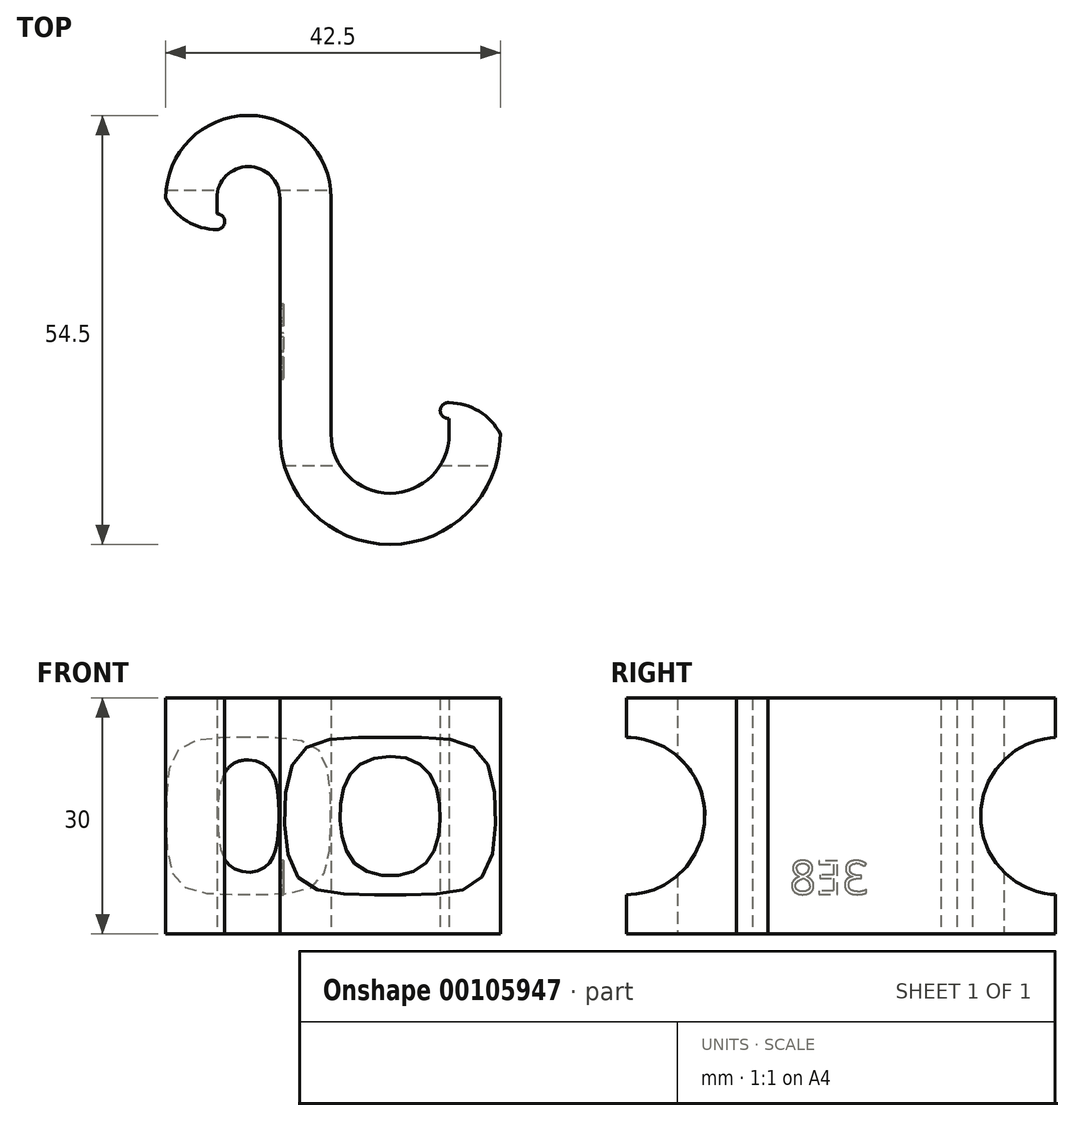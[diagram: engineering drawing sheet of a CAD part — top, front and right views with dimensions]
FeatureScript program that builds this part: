
annotation { "Feature Type Name" : "Feature", "Feature Type Description" : "" }
export const myFeature = defineFeature(function(context is Context, id is Id, definition is map)
    precondition{}
    {
        {
            var Q0;
            Q0=qCreatedBy(makeId("Top.planeOp"),FACE);
            var sketch = newSketch(context, id + "F0", { "sketchPlane" : qUnion([Q0])});
            skLineSegment(sketch, "E0", {"start": v(-4, 0) * mm, "end": v(4, 0) * mm, "construction": true});
            skLineSegment(sketch, "E1", {"start": v(-4, 0) * mm, "end": v(-4, -4) * mm, "construction": true});
            skArc(sketch, "E2", {"start": v(4, 0) * mm, "mid": v(0, 4) * mm, "end": v(-4, 0) * mm});
            skLineSegment(sketch, "E3", {"start": v(-4, -4) * mm, "end": v(-8, -4) * mm, "construction": true});
            skArc(sketch, "E4", {"start": v(10.5, 0) * mm, "mid": v(0, 10.5) * mm, "end": v(-10.5, 0) * mm});
            skLineSegment(sketch, "E5", {"start": v(10.5, 0) * mm, "end": v(10.5, -30) * mm});
            skLineSegment(sketch, "E6", {"start": v(4, -30) * mm, "end": v(10.5, -30) * mm, "construction": true});
            skArc(sketch, "E7", {"start": v(-4, -4) * mm, "mid": v(-3, -3) * mm, "end": v(-4, -2) * mm});
            skLineSegment(sketch, "E8", {"start": v(-4, -2) * mm, "end": v(-4, 0) * mm});
            skArc(sketch, "E9", {"start": v(-10.5, 0) * mm, "mid": v(-7.82, -2.92) * mm, "end": v(-4, -4) * mm});
            skLineSegment(sketch, "E10", {"start": v(4, 0) * mm, "end": v(4, -30) * mm});
            skArc(sketch, "E11", {"start": v(10.5, -30) * mm, "mid": v(18, -37.5) * mm, "end": v(25.5, -30) * mm});
            skArc(sketch, "E12", {"start": v(4, -30) * mm, "mid": v(18, -44) * mm, "end": v(32, -30) * mm});
            skLineSegment(sketch, "E13", {"start": v(25.5, -30) * mm, "end": v(25.5, -26) * mm, "construction": true});
            skArc(sketch, "E14", {"start": v(25.5, -26) * mm, "mid": v(24.38, -27) * mm, "end": v(25.5, -27.98) * mm});
            skLineSegment(sketch, "E15", {"start": v(25.5, -27.98) * mm, "end": v(25.5, -30) * mm});
            skArc(sketch, "E16", {"start": v(32, -30) * mm, "mid": v(29.32, -27.08) * mm, "end": v(25.5, -26) * mm});
            skSolve(sketch);
        }
        {
            var Q0;
            Q0=qSketchRegion(id+"F0",true);
            extrude(context, id + "F1", {"entities" : qUnion([Q0]), "depth" : 30 * mm});
        }
        {
            var Q0;
            Q0=makeQuery(id+"F1.opExtrude","SWEPT_FACE",FACE,{"disambiguationData":[OSD([sQuery(id+"F0.wireOp",EDGE,"E5")])]});
            var sketch = newSketch(context, id + "F2", { "sketchPlane" : qUnion([Q0])});
            skLineSegment(sketch, "E17", {"start": v(0, 0) * mm, "end": v(-30, 30) * mm, "construction": true});
            skPoint(sketch, "E18", {"position": v(-15, 15) * mm});
            skLineSegment(sketch, "E19", {"start": v(-15, 30) * mm, "end": v(-15, 0) * mm, "construction": true});
            skPoint(sketch, "E20", {"position": v(11, 15) * mm});
            skArc(sketch, "E21", {"start": v(11, 25) * mm, "mid": v(1, 15) * mm, "end": v(11, 5) * mm});
            skLineSegment(sketch, "E22", {"start": v(11, 25) * mm, "end": v(11, 5) * mm});
            skLineSegment(sketch, "E23", {"start": v(-15, 15) * mm, "end": v(11, 15) * mm, "construction": true});
            skLineSegment(sketch, "E24", {"start": v(-15, 15) * mm, "end": v(-44, 15) * mm, "construction": true});
            skLineSegment(sketch, "E25", {"start": v(-44, 25) * mm, "end": v(-44, 5) * mm});
            skArc(sketch, "E26", {"start": v(-44, 5) * mm, "mid": v(-34, 15) * mm, "end": v(-44, 25) * mm});
            skSolve(sketch);
        }
        {
            var Q0;
            Q0=qSketchRegion(id+"F2",true);
            extrude(context, id + "F3", {"entities" : qUnion([Q0]), "operationType" : NewBodyOperationType.REMOVE, "endBound" : BoundingType.THROUGH_ALL, "oppositeDirection" : true, "depth" : 25 * mm, "hasSecondDirection" : true, "secondDirectionBound" : SecondDirectionBoundingType.THROUGH_ALL, "secondDirectionOppositeDirection" : false, "secondDirectionDepth" : 25 * mm});
        }
        {
            var Q0;
            Q0=makeQuery(id+"F1.opExtrude","SWEPT_FACE",FACE,{"disambiguationData":[OSD([sQuery(id+"F0.wireOp",EDGE,"E10")])]});
            var sketch = newSketch(context, id + "F4", { "sketchPlane" : qUnion([Q0])});
            skText(sketch, "E27", { "text": "3E8", "fontName": "OpenSans-Regular.ttf"});
            const initialGuessF4  = {"E27": [0.0132, 0.00507, 1, 0, 0.00427]};
            skSetInitialGuess(sketch, initialGuessF4);
            skSolve(sketch);
        }
        {
            var Q0;
            Q0 = qSketchRegion(id + "F4", true);
            extrude(context, id + "F5", {"entities" : qUnion([Q0]), "operationType" : NewBodyOperationType.REMOVE, "oppositeDirection" : true, "depth" : .5 * mm});
        }
    });
